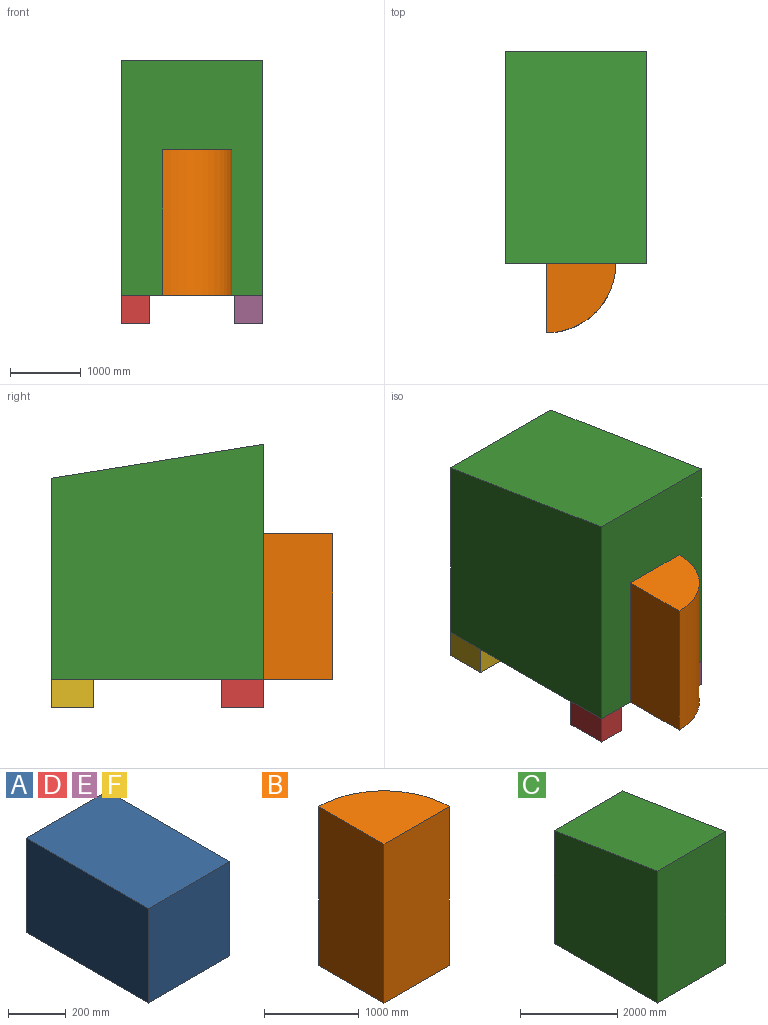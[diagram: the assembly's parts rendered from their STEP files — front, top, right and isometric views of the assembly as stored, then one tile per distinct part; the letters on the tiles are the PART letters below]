
ASSEMBLY  parts=6 mates=3
PART A: 6 faces, bbox 400x600x400 mm
  f0: plane 600x400mm, normal (-1,0,0), area 240000mm2, adj f1,f3,f4,f5
  f1: plane 400x400mm, normal (0,-1,0), area 160000mm2, adj f0,f2,f4,f5
  f2: plane 600x400mm, normal (1,0,0), area 240000mm2, adj f1,f3,f4,f5
  f3: plane 400x400mm, normal (0,1,0), area 160000mm2, adj f0,f2,f4,f5
  f4: plane 600x400mm, normal (0,0,1), area 240000mm2, adj f0,f1,f2,f3
  f5: plane 600x400mm, normal (0,0,-1), area 240000mm2, adj f0,f1,f2,f3
PART B: 5 faces, bbox 975x975x2057 mm
  f0: plane 2057x975mm, normal (0,-1,0), area 2005575mm2, adj f1,f2,f3,f4
  f1: cylinder r=975mm len=2057mm, axis (0,0,-1), area 3150349.8mm2, adj f0,f2,f3,f4
  f2: plane 2057x975mm, normal (-1,0,0), area 2005575mm2, adj f0,f1,f3,f4
  f3: plane 975x975mm, normal (0,0,1), area 746619.1mm2, adj f0,f1,f2
  f4: plane 975x975mm, normal (0,0,-1), area 746619.1mm2, adj f0,f1,f2
PART C: 6 faces, bbox 2000x3000x3320 mm
  f0: plane 3320x2000mm, normal (0,-1,0), area 6640000mm2, adj f1,f3,f4,f5
  f1: plane 3000x2000mm, normal (0,0,-1), area 6000000mm2, adj f0,f2,f4,f5
  f2: plane 2840x2000mm, normal (0,1,0), area 5680000mm2, adj f1,f3,f4,f5
  f3: plane 3000x2000mm, normal (0,0.16,0.99), area 6076314.7mm2, adj f0,f2,f4,f5
  f4: plane 3320x3000mm, normal (1,0,0), area 9240000mm2, adj f0,f1,f2,f3
  f5: plane 3320x3000mm, normal (-1,0,0), area 9240000mm2, adj f0,f1,f2,f3
PART D: same geometry as A
PART E: same geometry as A
PART F: same geometry as A
PLACE A t=(800,1200,-400)mm
PLACE B rot(axis=(0,0,-1),90deg) t=(-413.8,-1500,0)mm
PLACE C at identity
PLACE D t=(-800,-1200,-400)mm
PLACE E t=(800,-1200,-400)mm
PLACE F t=(-800,1200,-400)mm
MATE parallel B.f4 <-> C.f1  axis (0,0,-1) through (0,-1913.8,0)mm
MATE planar C.f0 <-> B.f2  axis (0,-1,0) through (0,-1500,1660)mm
MATE fastened D.f4 <-> C.f1  axis (0,0,1) through (-1000,-1500,0)mm
